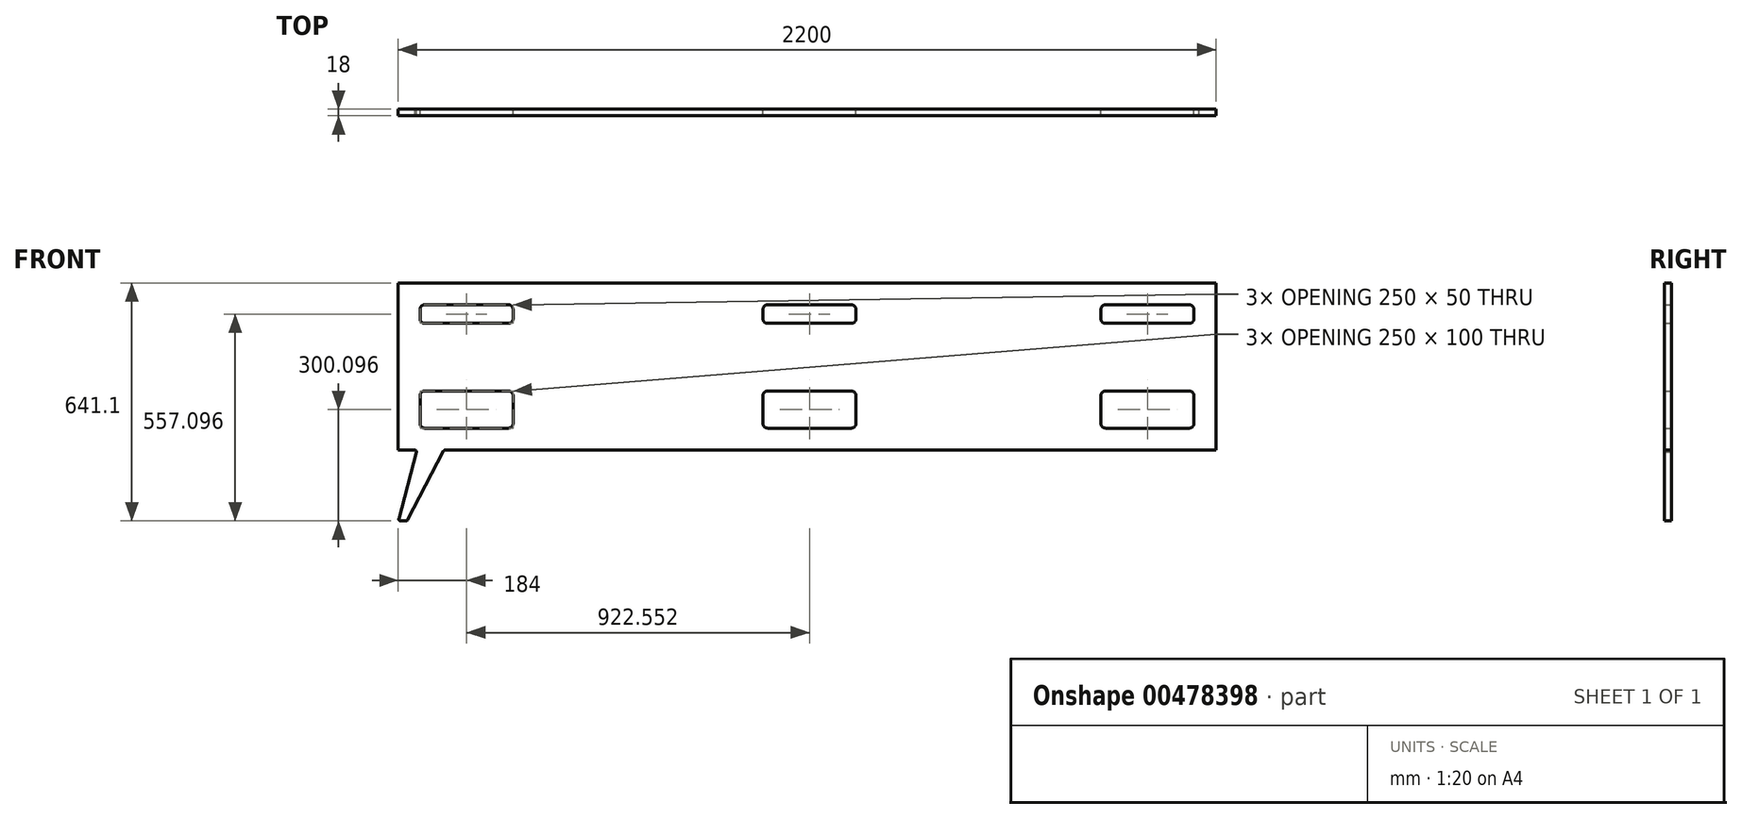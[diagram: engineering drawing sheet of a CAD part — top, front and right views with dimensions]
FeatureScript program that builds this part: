
annotation { "Feature Type Name" : "Feature", "Feature Type Description" : "" }
export const myFeature = defineFeature(function(context is Context, id is Id, definition is map)
    precondition{}
    {
        {
            var Q0;
            Q0=qCreatedBy(makeId("Front.planeOp"),FACE);
            var sketch = newSketch(context, id + "F0", { "sketchPlane" : qUnion([Q0])});
            skLineSegment(sketch, "E0.bottom", {"start": v(-1100, 75.88) * mm, "end": v(0, 75.88) * mm});
            skLineSegment(sketch, "E0.top", {"start": v(-1100, -374.12) * mm, "end": v(-1055, -374.12) * mm});
            skLineSegment(sketch, "E0.left", {"start": v(-1100, 75.88) * mm, "end": v(-1100, -374.12) * mm});
            skLineSegment(sketch, "E0.right", {"start": v(0, 25.88) * mm, "end": v(0, -324.06) * mm, "construction": true});
            skLineSegment(sketch, "E1", {"start": v(-1100, -374.12) * mm, "end": v(-1100, -565.22) * mm, "construction": true});
            skLineSegment(sketch, "E2", {"start": v(-1050, -374.12) * mm, "end": v(-1050, -374.12) * mm});
            skLineSegment(sketch, "E3", {"start": v(-1093.52, -565.22) * mm, "end": v(-1078.8, -565.22) * mm});
            skLineSegment(sketch, "E4", {"start": v(-1074.37, -562.53) * mm, "end": v(-977.78, -376.82) * mm});
            skPoint(sketch, "E5.visualSharp", {"position": v(-1100, -565.22) * mm});
            skArc(sketch, "E5.filletArc", {"start": v(-1098.36, -558.95) * mm, "mid": v(-1097.48, -563.28) * mm, "end": v(-1093.52, -565.22) * mm});
            skPoint(sketch, "E6.visualSharp", {"position": v(-1075.77, -565.22) * mm});
            skArc(sketch, "E6.filletArc", {"start": v(-1078.8, -565.22) * mm, "mid": v(-1076.21, -564.5) * mm, "end": v(-1074.37, -562.53) * mm});
            skLineSegment(sketch, "E7", {"start": v(-973.35, -374.12) * mm, "end": v(0, -374.12) * mm});
            skPoint(sketch, "E8.visualSharp", {"position": v(-976.38, -374.12) * mm});
            skArc(sketch, "E8.filletArc", {"start": v(-973.35, -374.12) * mm, "mid": v(-975.94, -374.85) * mm, "end": v(-977.78, -376.82) * mm});
            skArc(sketch, "E9", {"start": v(-1051.27, -378.96) * mm, "mid": v(-1051.86, -375.56) * mm, "end": v(-1055, -374.12) * mm});
            skLineSegment(sketch, "E10", {"start": v(-1051.27, -378.96) * mm, "end": v(-1098.36, -558.95) * mm});
            skArc(sketch, "E11.MirrorCS", {"start": v(1078.8, -565.22) * mm, "mid": v(1076.21, -564.5) * mm, "end": v(1074.37, -562.53) * mm});
            skLineSegment(sketch, "E12.MirrorCS", {"start": v(1093.52, -565.22) * mm, "end": v(1078.8, -565.22) * mm});
            skArc(sketch, "E13.MirrorCS", {"start": v(1098.36, -558.95) * mm, "mid": v(1097.48, -563.28) * mm, "end": v(1093.52, -565.22) * mm});
            skArc(sketch, "E14.MirrorCS", {"start": v(973.35, -374.12) * mm, "mid": v(975.94, -374.85) * mm, "end": v(977.78, -376.82) * mm});
            skArc(sketch, "E15.MirrorCS", {"start": v(1051.27, -378.96) * mm, "mid": v(1051.86, -375.56) * mm, "end": v(1055, -374.12) * mm});
            skPoint(sketch, "E16.MirrorP", {"position": v(1100, -565.22) * mm});
            skPoint(sketch, "E17.MirrorP", {"position": v(976.38, -374.12) * mm});
            skLineSegment(sketch, "E18.MirrorCS", {"start": v(1050, -374.12) * mm, "end": v(1050, -374.12) * mm});
            skLineSegment(sketch, "E19.MirrorCS", {"start": v(1074.37, -562.53) * mm, "end": v(977.78, -376.82) * mm});
            skLineSegment(sketch, "E20.MirrorCS", {"start": v(1100, 75.88) * mm, "end": v(1100, -374.12) * mm});
            skPoint(sketch, "E21.MirrorP", {"position": v(1075.77, -565.22) * mm});
            skLineSegment(sketch, "E22.MirrorCS", {"start": v(1100, -374.12) * mm, "end": v(1055, -374.12) * mm});
            skLineSegment(sketch, "E23.MirrorCS", {"start": v(1100, -374.12) * mm, "end": v(1100, -565.22) * mm, "construction": true});
            skLineSegment(sketch, "E24.MirrorCS", {"start": v(1051.27, -378.96) * mm, "end": v(1098.36, -558.95) * mm});
            skLineSegment(sketch, "E25.MirrorCS", {"start": v(1100, 75.88) * mm, "end": v(0, 75.88) * mm});
            skLineSegment(sketch, "E26.MirrorCS", {"start": v(973.35, -374.12) * mm, "end": v(0, -374.12) * mm});
            skPoint(sketch, "E27", {"position": v(0, 75.88) * mm});
            skPoint(sketch, "E28", {"position": v(-1100, 75.88) * mm});
            skLineSegment(sketch, "E29.0", {"start": v(-1100, 66.88) * mm, "end": v(0, 66.88) * mm});
            skLineSegment(sketch, "E30.0", {"start": v(-1091, 66.88) * mm, "end": v(-1091, -374.12) * mm});
            skLineSegment(sketch, "E31.0", {"start": v(-1100, -365.12) * mm, "end": v(0, -365.12) * mm});
            skLineSegment(sketch, "E32.MirrorCS", {"start": v(1100, 66.88) * mm, "end": v(0, 66.88) * mm});
            skLineSegment(sketch, "E33.MirrorCS", {"start": v(1091, -365.12) * mm, "end": v(0, -365.12) * mm});
            skLineSegment(sketch, "E34.MirrorCS", {"start": v(1091, 75.88) * mm, "end": v(1091, -365.04) * mm});
            skLineSegment(sketch, "E35", {"start": v(-1055, -374.12) * mm, "end": v(-973.35, -374.12) * mm});
            skLineSegment(sketch, "E36.MirrorCS", {"start": v(1055, -374.12) * mm, "end": v(973.35, -374.12) * mm});
            skLineSegment(sketch, "E37", {"start": v(1091, -365.04) * mm, "end": v(1091, -365.12) * mm});
            skPoint(sketch, "E38.end.orphan", {"position": v(1091, -374.12) * mm});
            skPoint(sketch, "E39.orphan", {"position": v(1100, -365.12) * mm});
            skLineSegment(sketch, "E40", {"start": v(973.35, -374.12) * mm, "end": v(973.35, -365.12) * mm, "construction": true});
            skPoint(sketch, "E41.orphan", {"position": v(-1091, 75.88) * mm});
            skLineSegment(sketch, "E42.bottom", {"start": v(-1041, -215.12) * mm, "end": v(-791, -215.12) * mm, "construction": true});
            skLineSegment(sketch, "E42.top", {"start": v(-1041, -315.12) * mm, "end": v(-791, -315.12) * mm, "construction": true});
            skLineSegment(sketch, "E42.left", {"start": v(-1041, -215.12) * mm, "end": v(-1041, -315.12) * mm, "construction": true});
            skLineSegment(sketch, "E42.right", {"start": v(-791, -215.12) * mm, "end": v(-791, -315.12) * mm, "construction": true});
            skLineSegment(sketch, "E43.bottom", {"start": v(-1041, 16.88) * mm, "end": v(-791, 16.88) * mm, "construction": true});
            skLineSegment(sketch, "E43.top", {"start": v(-1041, -33.12) * mm, "end": v(-791, -33.12) * mm, "construction": true});
            skLineSegment(sketch, "E43.left", {"start": v(-1041, 16.88) * mm, "end": v(-1041, -33.12) * mm, "construction": true});
            skLineSegment(sketch, "E43.right", {"start": v(-791, 16.88) * mm, "end": v(-791, -33.12) * mm, "construction": true});
            skLineSegment(sketch, "E44.bottom", {"start": v(-1029, -215.12) * mm, "end": v(-803, -215.12) * mm});
            skLineSegment(sketch, "E44.top", {"start": v(-1029, -315.12) * mm, "end": v(-803, -315.12) * mm});
            skLineSegment(sketch, "E44.left", {"start": v(-1041, -227.12) * mm, "end": v(-1041, -303.12) * mm});
            skLineSegment(sketch, "E44.right", {"start": v(-791, -227.12) * mm, "end": v(-791, -303.12) * mm});
            skPoint(sketch, "E45.visualSharp", {"position": v(-1041, -215.12) * mm});
            skArc(sketch, "E45.filletArc", {"start": v(-1029, -215.12) * mm, "mid": v(-1037.49, -218.64) * mm, "end": v(-1041, -227.12) * mm});
            skPoint(sketch, "E46.visualSharp", {"position": v(-1041, -315.12) * mm});
            skArc(sketch, "E46.filletArc", {"start": v(-1041, -303.12) * mm, "mid": v(-1037.49, -311.6) * mm, "end": v(-1029, -315.12) * mm});
            skPoint(sketch, "E47.visualSharp", {"position": v(-791, -315.12) * mm});
            skArc(sketch, "E47.filletArc", {"start": v(-803, -315.12) * mm, "mid": v(-794.51, -311.6) * mm, "end": v(-791, -303.12) * mm});
            skPoint(sketch, "E48.visualSharp", {"position": v(-791, -215.12) * mm});
            skArc(sketch, "E48.filletArc", {"start": v(-791, -227.12) * mm, "mid": v(-794.51, -218.64) * mm, "end": v(-803, -215.12) * mm});
            skLineSegment(sketch, "E49.bottom", {"start": v(-1029, 16.88) * mm, "end": v(-803, 16.88) * mm});
            skLineSegment(sketch, "E49.top", {"start": v(-1029, -33.12) * mm, "end": v(-803, -33.12) * mm});
            skLineSegment(sketch, "E49.left", {"start": v(-1041, 4.88) * mm, "end": v(-1041, -21.12) * mm});
            skLineSegment(sketch, "E49.right", {"start": v(-791, 4.88) * mm, "end": v(-791, -21.12) * mm});
            skPoint(sketch, "E50.visualSharp", {"position": v(-1041, 16.88) * mm});
            skArc(sketch, "E50.filletArc", {"start": v(-1029, 16.88) * mm, "mid": v(-1037.49, 13.36) * mm, "end": v(-1041, 4.88) * mm});
            skPoint(sketch, "E51.visualSharp", {"position": v(-1041, -33.12) * mm});
            skArc(sketch, "E51.filletArc", {"start": v(-1041, -21.12) * mm, "mid": v(-1037.49, -29.6) * mm, "end": v(-1029, -33.12) * mm});
            skPoint(sketch, "E52.visualSharp", {"position": v(-791, -33.12) * mm});
            skArc(sketch, "E52.filletArc", {"start": v(-803, -33.12) * mm, "mid": v(-794.51, -29.6) * mm, "end": v(-791, -21.12) * mm});
            skPoint(sketch, "E53.visualSharp", {"position": v(-791, 16.88) * mm});
            skArc(sketch, "E53.filletArc", {"start": v(-791, 4.88) * mm, "mid": v(-794.51, 13.36) * mm, "end": v(-803, 16.88) * mm});
            skLineSegment(sketch, "E54.MirrorCS", {"start": v(791, -227.12) * mm, "end": v(791, -303.12) * mm});
            skLineSegment(sketch, "E55.MirrorCS", {"start": v(1041, -227.12) * mm, "end": v(1041, -303.12) * mm});
            skLineSegment(sketch, "E56.MirrorCS", {"start": v(1029, -215.12) * mm, "end": v(803, -215.12) * mm});
            skLineSegment(sketch, "E57.MirrorCS", {"start": v(1029, -315.12) * mm, "end": v(803, -315.12) * mm});
            skLineSegment(sketch, "E58.MirrorCS", {"start": v(1041, -215.12) * mm, "end": v(1041, -315.12) * mm, "construction": true});
            skArc(sketch, "E59.MirrorCS", {"start": v(1029, -215.12) * mm, "mid": v(1037.49, -218.64) * mm, "end": v(1041, -227.12) * mm});
            skLineSegment(sketch, "E60.MirrorCS", {"start": v(791, -215.12) * mm, "end": v(791, -315.12) * mm, "construction": true});
            skLineSegment(sketch, "E61.MirrorCS", {"start": v(1041, -315.12) * mm, "end": v(791, -315.12) * mm, "construction": true});
            skArc(sketch, "E62.MirrorCS", {"start": v(803, -315.12) * mm, "mid": v(794.51, -311.6) * mm, "end": v(791, -303.12) * mm});
            skArc(sketch, "E63.MirrorCS", {"start": v(1041, -303.12) * mm, "mid": v(1037.49, -311.6) * mm, "end": v(1029, -315.12) * mm});
            skPoint(sketch, "E64.MirrorP", {"position": v(791, -315.12) * mm});
            skPoint(sketch, "E65.MirrorP", {"position": v(791, -215.12) * mm});
            skPoint(sketch, "E66.MirrorP", {"position": v(1041, -215.12) * mm});
            skArc(sketch, "E67.MirrorCS", {"start": v(791, -227.12) * mm, "mid": v(794.51, -218.64) * mm, "end": v(803, -215.12) * mm});
            skLineSegment(sketch, "E68.MirrorCS", {"start": v(1041, -215.12) * mm, "end": v(791, -215.12) * mm, "construction": true});
            skPoint(sketch, "E69.MirrorP", {"position": v(1041, -315.12) * mm});
            skArc(sketch, "E70.MirrorCS", {"start": v(1029, 16.88) * mm, "mid": v(1037.49, 13.36) * mm, "end": v(1041, 4.88) * mm});
            skArc(sketch, "E71.MirrorCS", {"start": v(1041, -21.12) * mm, "mid": v(1037.49, -29.6) * mm, "end": v(1029, -33.12) * mm});
            skArc(sketch, "E72.MirrorCS", {"start": v(803, -33.12) * mm, "mid": v(794.51, -29.6) * mm, "end": v(791, -21.12) * mm});
            skLineSegment(sketch, "E73.MirrorCS", {"start": v(791, 4.88) * mm, "end": v(791, -21.12) * mm});
            skArc(sketch, "E74.MirrorCS", {"start": v(791, 4.88) * mm, "mid": v(794.51, 13.36) * mm, "end": v(803, 16.88) * mm});
            skLineSegment(sketch, "E75.MirrorCS", {"start": v(1041, 4.88) * mm, "end": v(1041, -21.12) * mm});
            skLineSegment(sketch, "E76.MirrorCS", {"start": v(1029, -33.12) * mm, "end": v(803, -33.12) * mm});
            skLineSegment(sketch, "E77.MirrorCS", {"start": v(1029, 16.88) * mm, "end": v(803, 16.88) * mm});
            skPoint(sketch, "E78.MirrorP", {"position": v(791, -33.12) * mm});
            skLineSegment(sketch, "E79.MirrorCS", {"start": v(1041, -33.12) * mm, "end": v(791, -33.12) * mm, "construction": true});
            skLineSegment(sketch, "E80.MirrorCS", {"start": v(1041, 16.88) * mm, "end": v(791, 16.88) * mm, "construction": true});
            skPoint(sketch, "E81.MirrorP", {"position": v(791, 16.88) * mm});
            skLineSegment(sketch, "E82.MirrorCS", {"start": v(1041, 16.88) * mm, "end": v(1041, -33.12) * mm, "construction": true});
            skLineSegment(sketch, "E83.MirrorCS", {"start": v(791, 16.88) * mm, "end": v(791, -33.12) * mm, "construction": true});
            skPoint(sketch, "E84.MirrorP", {"position": v(1041, 16.88) * mm});
            skPoint(sketch, "E85.MirrorP", {"position": v(1041, -33.12) * mm});
            skLineSegment(sketch, "E86.bottom", {"start": v(-118.45, -215.12) * mm, "end": v(131.55, -215.12) * mm, "construction": true});
            skLineSegment(sketch, "E86.top", {"start": v(-118.45, -315.12) * mm, "end": v(131.55, -315.12) * mm, "construction": true});
            skLineSegment(sketch, "E86.left", {"start": v(-118.45, -215.12) * mm, "end": v(-118.45, -315.12) * mm, "construction": true});
            skLineSegment(sketch, "E86.right", {"start": v(131.55, -215.12) * mm, "end": v(131.55, -315.12) * mm, "construction": true});
            skLineSegment(sketch, "E87.bottom", {"start": v(-118.45, 16.88) * mm, "end": v(131.55, 16.88) * mm, "construction": true});
            skLineSegment(sketch, "E87.top", {"start": v(-118.45, -33.12) * mm, "end": v(131.55, -33.12) * mm, "construction": true});
            skLineSegment(sketch, "E87.left", {"start": v(-118.45, 16.88) * mm, "end": v(-118.45, -33.12) * mm, "construction": true});
            skLineSegment(sketch, "E87.right", {"start": v(131.55, 16.88) * mm, "end": v(131.55, -33.12) * mm, "construction": true});
            skLineSegment(sketch, "E88.bottom", {"start": v(-106.45, -215.12) * mm, "end": v(119.55, -215.12) * mm});
            skLineSegment(sketch, "E88.top", {"start": v(-106.45, -315.12) * mm, "end": v(119.55, -315.12) * mm});
            skLineSegment(sketch, "E88.left", {"start": v(-118.45, -227.12) * mm, "end": v(-118.45, -303.12) * mm});
            skLineSegment(sketch, "E88.right", {"start": v(131.55, -227.12) * mm, "end": v(131.55, -303.12) * mm});
            skPoint(sketch, "E89.visualSharp", {"position": v(-118.45, -215.12) * mm});
            skArc(sketch, "E89.filletArc", {"start": v(-106.45, -215.12) * mm, "mid": v(-114.93, -218.64) * mm, "end": v(-118.45, -227.12) * mm});
            skPoint(sketch, "E90.visualSharp", {"position": v(-118.45, -315.12) * mm});
            skArc(sketch, "E90.filletArc", {"start": v(-118.45, -303.12) * mm, "mid": v(-114.93, -311.6) * mm, "end": v(-106.45, -315.12) * mm});
            skPoint(sketch, "E91.visualSharp", {"position": v(131.55, -315.12) * mm});
            skArc(sketch, "E91.filletArc", {"start": v(119.55, -315.12) * mm, "mid": v(128.04, -311.6) * mm, "end": v(131.55, -303.12) * mm});
            skPoint(sketch, "E92.visualSharp", {"position": v(131.55, -215.12) * mm});
            skArc(sketch, "E92.filletArc", {"start": v(131.55, -227.12) * mm, "mid": v(128.04, -218.64) * mm, "end": v(119.55, -215.12) * mm});
            skLineSegment(sketch, "E93.bottom", {"start": v(-106.45, 16.88) * mm, "end": v(119.55, 16.88) * mm});
            skLineSegment(sketch, "E93.top", {"start": v(-106.45, -33.12) * mm, "end": v(119.55, -33.12) * mm});
            skLineSegment(sketch, "E93.left", {"start": v(-118.45, 4.88) * mm, "end": v(-118.45, -21.12) * mm});
            skLineSegment(sketch, "E93.right", {"start": v(131.55, 4.88) * mm, "end": v(131.55, -21.12) * mm});
            skPoint(sketch, "E94.visualSharp", {"position": v(-118.45, 16.88) * mm});
            skArc(sketch, "E94.filletArc", {"start": v(-106.45, 16.88) * mm, "mid": v(-114.93, 13.36) * mm, "end": v(-118.45, 4.88) * mm});
            skPoint(sketch, "E95.visualSharp", {"position": v(-118.45, -33.12) * mm});
            skArc(sketch, "E95.filletArc", {"start": v(-118.45, -21.12) * mm, "mid": v(-114.93, -29.6) * mm, "end": v(-106.45, -33.12) * mm});
            skPoint(sketch, "E96.visualSharp", {"position": v(131.55, -33.12) * mm});
            skArc(sketch, "E96.filletArc", {"start": v(119.55, -33.12) * mm, "mid": v(128.04, -29.6) * mm, "end": v(131.55, -21.12) * mm});
            skPoint(sketch, "E97.visualSharp", {"position": v(131.55, 16.88) * mm});
            skArc(sketch, "E97.filletArc", {"start": v(131.55, 4.88) * mm, "mid": v(128.04, 13.36) * mm, "end": v(119.55, 16.88) * mm});
            skSolve(sketch);
        }
        {
            var Q0;
            {var subQ0=sQuery(id+"F0.wireOp",EDGE,"E0.left");var subQ1=sQuery(id+"F0.wireOp",EDGE,"E0.bottom");var subQ2=makeQuery(id+"F0.imprint","INTERSECT",VERTEX,{"derivedFrom":[subQ1,subQ0]});Q0=makeQuery(id+"F0.imprint","IMPRINT",FACE,{"disambiguationData":[TD([[makeQuery(id+"F0.imprint","IMPRINT",EDGE,{"disambiguationData":[TD([[subQ2,-1.0]])],"derivedFrom":subQ1}),-1.0]])]});}
            var Q1;
            Q1=makeQuery(id+"F0.imprint","IMPRINT",FACE,{"disambiguationData":[TD([[makeQuery(id+"F0.imprint","IMPRINT",EDGE,{"derivedFrom":sQuery(id+"F0.wireOp",EDGE,"phRE26gc-SDI3-kEnA-uSIr-O7jfQECWDf2I.bottom")}),1.0]])]});
            var Q2;
            Q2=makeQuery(id+"F0.imprint","IMPRINT",FACE,{"disambiguationData":[TD([[makeQuery(id+"F0.imprint","IMPRINT",EDGE,{"derivedFrom":sQuery(id+"F0.wireOp",EDGE,"E3")}),1.0]])]});
            var Q3;
            {var subQ0=sQuery(id+"F0.wireOp",EDGE,"E32.MirrorCS");var subQ1=sQuery(id+"F0.wireOp",EDGE,"E20.MirrorCS");var subQ2=makeQuery(id+"F0.imprint","INTERSECT",VERTEX,{"derivedFrom":[subQ1,subQ0]});Q3=makeQuery(id+"F0.imprint","IMPRINT",FACE,{"disambiguationData":[TD([[makeQuery(id+"F0.imprint","IMPRINT",EDGE,{"disambiguationData":[TD([[subQ2,-1.0]])],"derivedFrom":subQ1}),-1.0]])]});}
            var Q4;
            {var subQ1=sQuery(id+"F0.wireOp",EDGE,"E0.bottom");var subQ7=sQuery(id+"F0.wireOp",EDGE,"E25.MirrorCS");var subQ8=makeQuery(id+"F0.imprint","INTERSECT",VERTEX,{"derivedFrom":[subQ1,subQ7]});Q4=makeQuery(id+"F0.imprint","IMPRINT",FACE,{"disambiguationData":[TD([[makeQuery(id+"F0.imprint","IMPRINT",EDGE,{"disambiguationData":[TD([[subQ8,1.0]])],"derivedFrom":subQ1}),-1.0]])]});}
            var Q5;
            {var subQ0=sQuery(id+"F0.wireOp",EDGE,"E29.0");var subQ1=sQuery(id+"F0.wireOp",EDGE,"E0.left");var subQ2=makeQuery(id+"F0.imprint","INTERSECT",VERTEX,{"derivedFrom":[subQ1,subQ0]});Q5=makeQuery(id+"F0.imprint","IMPRINT",FACE,{"disambiguationData":[TD([[makeQuery(id+"F0.imprint","IMPRINT",EDGE,{"disambiguationData":[TD([[subQ2,-1.0]])],"derivedFrom":subQ1}),1.0]])]});}
            var Q6;
            {var subQ0=sQuery(id+"F0.wireOp",EDGE,"E0.left");var subQ1=sQuery(id+"F0.wireOp",EDGE,"E0.top");var subQ2=makeQuery(id+"F0.imprint","INTERSECT",VERTEX,{"derivedFrom":[subQ1,subQ0]});Q6=makeQuery(id+"F0.imprint","IMPRINT",FACE,{"disambiguationData":[TD([[makeQuery(id+"F0.imprint","IMPRINT",EDGE,{"disambiguationData":[TD([[subQ2,-1.0]])],"derivedFrom":subQ1}),1.0]])]});}
            var Q7;
            {var subQ0=sQuery(id+"F0.wireOp",EDGE,"E20.MirrorCS");var subQ1=sQuery(id+"F0.wireOp",EDGE,"E25.MirrorCS");var subQ2=makeQuery(id+"F0.imprint","INTERSECT",VERTEX,{"derivedFrom":[subQ1,subQ0]});Q7=makeQuery(id+"F0.imprint","IMPRINT",FACE,{"disambiguationData":[TD([[makeQuery(id+"F0.imprint","IMPRINT",EDGE,{"disambiguationData":[TD([[subQ2,-1.0]])],"derivedFrom":subQ1}),1.0]])]});}
            var Q8;
            {var subQ0=sQuery(id+"F0.wireOp",EDGE,"E22.MirrorCS");var subQ1=sQuery(id+"F0.wireOp",EDGE,"E20.MirrorCS");var subQ2=makeQuery(id+"F0.imprint","INTERSECT",VERTEX,{"derivedFrom":[subQ1,subQ0]});Q8=makeQuery(id+"F0.imprint","IMPRINT",FACE,{"disambiguationData":[TD([[makeQuery(id+"F0.imprint","IMPRINT",EDGE,{"disambiguationData":[TD([[subQ2,1.0]])],"derivedFrom":subQ1}),-1.0]])]});}
            var Q9;
            Q9=makeQuery(id+"F0.imprint","IMPRINT",FACE,{"disambiguationData":[TD([[makeQuery(id+"F0.imprint","IMPRINT",EDGE,{"derivedFrom":sQuery(id+"F0.wireOp",EDGE,"E11.MirrorCS")}),-1.0]])]});
            var Q10;
            {var subQ10=sQuery(id+"F0.wireOp",EDGE,"phRE26gc-SDI3-kEnA-uSIr-O7jfQECWDf2I.left");Q10=makeQuery(id+"F0.imprint","IMPRINT",FACE,{"disambiguationData":[TD([[makeQuery(id+"F0.imprint","IMPRINT",EDGE,{"derivedFrom":subQ10}),-1.0]])]});}
            var Q11;
            {var subQ0=sQuery(id+"F0.wireOp",EDGE,"E33.MirrorCS");Q11=makeQuery(id+"F0.imprint","IMPRINT",FACE,{"disambiguationData":[TD([[makeQuery(id+"F0.imprint","IMPRINT",EDGE,{"derivedFrom":subQ0}),-1.0]])]});}
            extrude(context, id + "F1", {"entities" : qUnion([Q0, Q1, Q2, Q3, Q4, Q5, Q6, Q7, Q8, Q9, Q10, Q11]), "depth" : 18 * mm});
        }
    });
